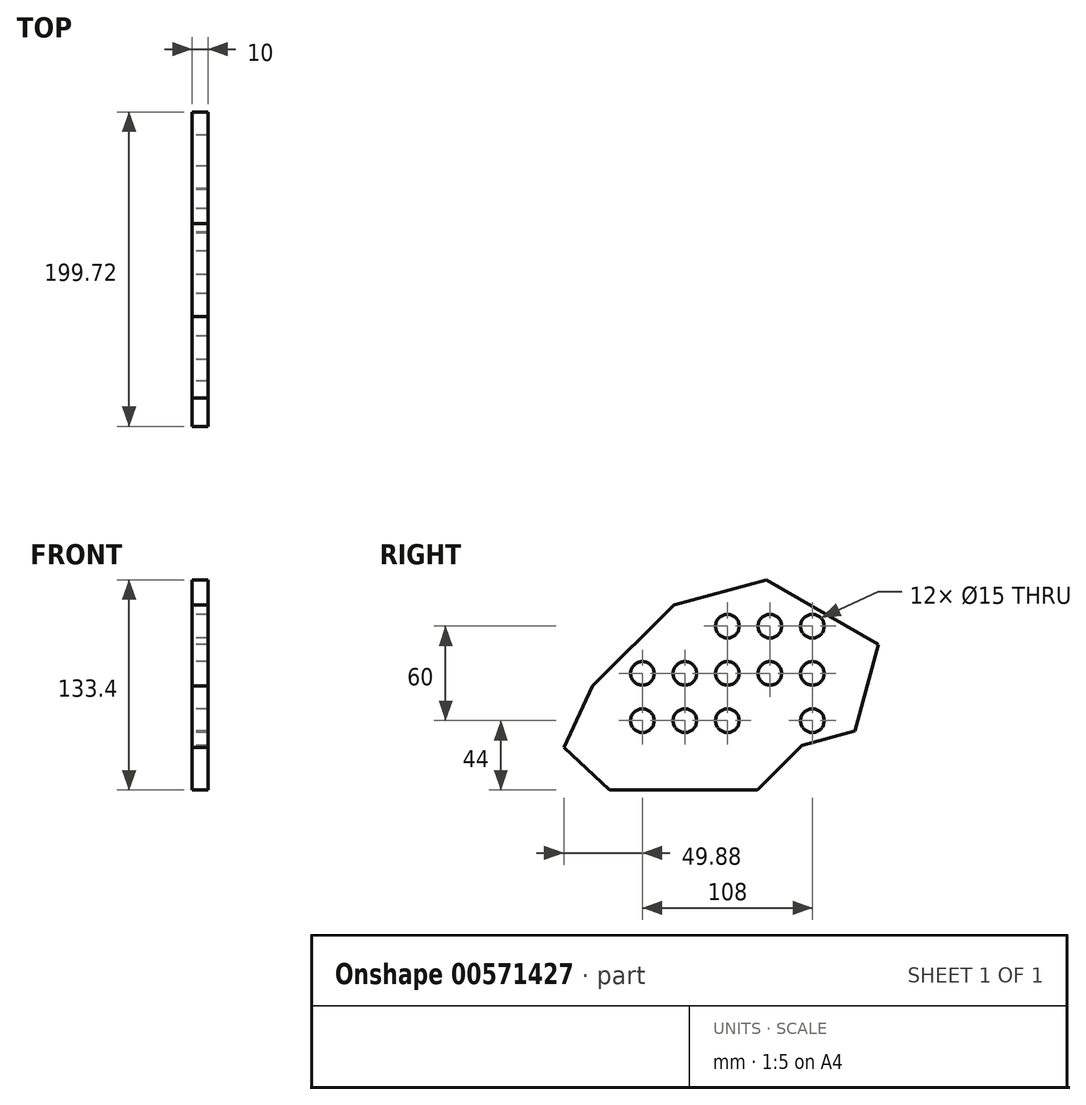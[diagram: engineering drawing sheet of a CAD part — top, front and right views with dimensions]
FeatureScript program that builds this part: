
annotation { "Feature Type Name" : "Feature", "Feature Type Description" : "" }
export const myFeature = defineFeature(function(context is Context, id is Id, definition is map)
    precondition{}
    {
        {
            var Q0;
            Q0=qCreatedBy(makeId("Right.planeOp"),FACE);
            var sketch = newSketch(context, id + "F0", { "sketchPlane" : qUnion([Q0])});
            skLineSegment(sketch, "E0", {"start": v(73, 0) * mm, "end": v(101.28, 28.28) * mm});
            skLineSegment(sketch, "E1", {"start": v(101.28, 28.28) * mm, "end": v(135.1, 37.34) * mm});
            skLineSegment(sketch, "E2", {"start": v(135.1, 37.34) * mm, "end": v(149.84, 92.4) * mm});
            skLineSegment(sketch, "E3", {"start": v(149.84, 92.4) * mm, "end": v(78.83, 133.4) * mm});
            skLineSegment(sketch, "E4", {"start": v(78.83, 133.4) * mm, "end": v(19.9, 117.61) * mm});
            skLineSegment(sketch, "E5", {"start": v(-49.88, 27.02) * mm, "end": v(-21, 0) * mm});
            skLineSegment(sketch, "E6", {"start": v(19.9, 117.61) * mm, "end": v(-31.7, 66) * mm});
            skLineSegment(sketch, "E7", {"start": v(-31.7, 66) * mm, "end": v(-49.88, 27.02) * mm});
            skLineSegment(sketch, "E8", {"start": v(-21, 0) * mm, "end": v(73, 0) * mm});
            skCircle(sketch, "E9", {"center": v(0, 44) * mm, "radius": 7.5 * mm});
            skCircle(sketch, "E10.0.1.0", {"center": v(0, 74) * mm, "radius": 7.5 * mm});
            skCircle(sketch, "E10.1.0.0", {"center": v(27, 44) * mm, "radius": 7.5 * mm});
            skCircle(sketch, "E10.1.1.0", {"center": v(27, 74) * mm, "radius": 7.5 * mm});
            skCircle(sketch, "E10.2.0.0", {"center": v(54, 44) * mm, "radius": 7.5 * mm});
            skCircle(sketch, "E10.2.1.0", {"center": v(54, 74) * mm, "radius": 7.5 * mm});
            skCircle(sketch, "E10.2.2.0", {"center": v(54, 104) * mm, "radius": 7.5 * mm});
            skCircle(sketch, "E10.3.1.0", {"center": v(81, 74) * mm, "radius": 7.5 * mm});
            skCircle(sketch, "E10.3.2.0", {"center": v(81, 104) * mm, "radius": 7.5 * mm});
            skCircle(sketch, "E10.4.0.0", {"center": v(108, 44) * mm, "radius": 7.5 * mm});
            skCircle(sketch, "E10.4.1.0", {"center": v(108, 74) * mm, "radius": 7.5 * mm});
            skCircle(sketch, "E10.4.2.0", {"center": v(108, 104) * mm, "radius": 7.5 * mm});
            skLineSegment(sketch, "E10.direction1", {"start": v(0, 44) * mm, "end": v(27, 44) * mm, "construction": true});
            skLineSegment(sketch, "E10.direction2", {"start": v(0, 44) * mm, "end": v(0, 74) * mm, "construction": true});
            skSolve(sketch);
        }
        {
            var Q0;
            Q0=makeQuery(id+"F0.imprint","IMPRINT",FACE,{"disambiguationData":[TD([[makeQuery(id+"F0.imprint","IMPRINT",EDGE,{"derivedFrom":sQuery(id+"F0.wireOp",EDGE,"E0")}),1.0]])]});
            extrude(context, id + "F1", {"entities" : qUnion([Q0]), "depth" : 10 * mm, "offsetDistance" : 25 * mm});
        }
    });
